# Revit family: Building-ContenitoriParete-GEWISS-44CEP-PANNELLI_DIN_1X
name_source: partatom
category: Apparecchi elettrici
revit_build: Autodesk Revit 2016 (Build: 20161004_0715(x64)
units: mm (PartAtom-declared; Revit-internal decimal feet)

## family parameters
Basato su piano di lavoro = Sì
Condiviso = No
Mantenere orientamento annotazione = No
Numero OmniClass = 23.80.30.11.17
Punto di calcolo locali = Sì
Quota connettore circolare = Usa diametro
Sempre verticale = No
Taglio con vuoti quando caricato = No
Tipo di parte = Normale
Titolo OmniClass = Distribution Boards and Control Panels

## types (2) — shared parameters
Altezza = 356 mm  [stored 1.16798 ft]
Caratteristiche = Halogen free
Catalogo = BUILDING
Catalogo Serie = 44 CEP
Codice Electrocod = 1310
Colore = Grigio RAL 7035
Cornice = GEWISS - GRIGIO
GEWISS SCHEDA TECNICA = http://pro.gewiss.com
H_da terra = 547 mm
IDF = e5b4c7fc-f8a6-4209-b309-5f046737254a
IDT = 6b5b4bd3-b3c6-410c-8e2b-0edb16ce71f3
Immagine tipo = GW44852.jpg
Larghezza foro = 252 mm  [stored 0.826772 ft]
Lunghezza = 276 mm  [stored 0.905512 ft]
Pannello = GEWISS - GRIGIO RAL 7035
Per quadri: = 44 CEP
Produttore = GEWISS S.p.A.
Prospetto di default = 1219 mm
SEO = Pannello
Scheda Tecnica = https://www.gewiss.com
Spessore = 5 mm  [stored 0.0164042 ft]
Tipo Materiale = Halogen free secondo norma EN 50267-2-2
URL = https://www.gewiss.com
Versione file RFA = 18.0
Voltaggio = NP
Watt = NP

## per-type parameters (varying)
| type | Adatto per | Codice EAN | Descrizione | Modello | N. mod. EN 50022 | N. mod. EN 50022: | Per quadri BxH (mm) |
| GW44852 - PANNELLO FRONTALE FIN.8M.CEP 236X316 | Scatolati max125 A | 8011564111332 | PANNELLO FRONTALE FIN.8M.CEP 236X316 | GW44852 | 8 | 8 | 236x316 |
| GW44853 - PANNELLO FRONTALE FIN.14M.CEP 316X396 | Scatolati max160 A | 8011564111349 | PANNELLO FRONTALE FIN.14M.CEP 316X396 | GW44853 | 14 | 14 | 316x396 |

note: [stored X ft] marks values corroborated as IEEE doubles in the binary element streams (Revit-internal decimal feet)

## geometry (parser evidence)
native form markers: Blend x2
no freeform markers — native parametric forms only
